# Revit family: PRD_AR_SpprtRls_MEDCAREGrabRail_MEDC0009_MEDC0010_MEDC0011_MEDC0012
name_source: partatom
category: Specialty Equipment
units: mm (PartAtom-declared; Revit-internal decimal feet)

## family parameters
Cut with Voids When Loaded = No
Enable Cutting in Views = No
Host = Face
Maintain Annotation Orientation = No
OmniClass Number = 23.40.20.21.47
OmniClass Title = Bath Grab Bars
Part Type = Normal
Room Calculation Point = No
Round Connector Dimension = Use Diameter
Shared = No

## types (4) — shared parameters
AssetType = Fixed
Back = no
BodyMaterial = PRD_AR_StainlessSteel_SatinFinished_BasaltGrey
Category = Pr_40_20_76_84, Support rails
Color = basalt grey
Default Elevation = 1200 mm
Diameter = 32 mm  [stored 0.104987 ft]
Export Type to IFC As = IfcRailingType
Finish = satin finished
IfcExportAs = IfcRailingType
IfcExportType = HANDRAIL
IsExternal = FALSE
Manufacturer = KWC Group Management AG
ManufacturerName = KWC Group Management AG
ManufacturerURL = www.kwc-professional.com
Material = stainless steel
MaterialCode = 1.4301 Chrome Nickel steel V2A
NBSDescription = Support rails
NBSReference = 45-35-72/360
NominalHeight = 234 mm  [stored 0.767717 ft]
NominalWidth = 113 mm  [stored 0.370735 ft]
OverallHeight = 234 mm
OverallWidth = 113 mm
ProductInformation = http://pim.kwc.com
Status = New
SurfaceFinish = satin finished
Type IFC Predefined Type = HANDRAIL
TypeOfFixing = screw
TypeOfGrabRail = support bar
TypeOfMounting = wall mounting
URL = www.kwc-professional.com
Uniclass2015Code = Pr_40_20_76_84
Uniclass2015Title = Support rails
Uniclass2015Version = Products v1.36
Version = 1
zero-valued in all types: Height

## per-type parameters (varying)
| type | BIMObjectName | Depth | Description | ElectronicFlushActuation | Features | ModelNumber | Name | NominalDepth | OverallDepth | Size |
| MEDC0009 | PRD_AR_SupportRails_MEDCAREFoldingSupportRail_MEDC0009 | 700 mm  [stored 2.29659 ft] | MEDCARE folding support rail with toilet roll holder for wall mounting, stainless steel, basalt grey coated surface, two parallel rail levels, top rail 32 mm, bottom rail 27 mm, material thickness 1.5 mm, plastic end caps, protection against accidental folding, stainless steel mounting plate with basalt grey polyamide cover, load capacity up to 150 kg, mounting material to be provided by client. | No | With toilet roll holder. Load capacity up to 150 kg. Length 700 mm. | 3600003778 | MEDCARE Folding support rail MEDC0009 | 700 mm  [stored 2.29659 ft] | 700 mm | 113 x 234 x 700 mm (W x H x D) |
| MEDC0010 | PRD_AR_SupportRails_MEDCAREFoldingSupportRail_MEDC0010 | 850 mm  [stored 2.78871 ft] | MEDCARE folding support rail with toilet roll holder for wall mounting, stainless steel, basalt grey coated surface, two parallel rail levels, top rail 32 mm, bottom rail 27 mm, material thickness 1.5 mm, plastic end caps, protection against accidental folding, stainless steel mounting plate with basalt grey polyamide cover, load capacity up to 100 kg, mounting material to be provided by client. | No | With toilet roll holder. Load capacity up to 100 kg. Length 850 mm. | 3600003780 | MEDCARE Folding support rail MEDC0010 | 850 mm  [stored 2.78871 ft] | 850 mm | 113 x 234 x 850 mm (W x H x D) |
| MEDC0011 | PRD_AR_SupportRails_MEDCAREFoldingSupportRail_MEDC0011 | 700 mm  [stored 2.29659 ft] | MEDCARE folding support rail with electronic flush actuation, for wall mounting, stainless steel, basalt grey coated surface, two parallel rail levels, upper rail 32 mm, lower rail 27 mm, material thickness 1.5 mm, with plastic end caps and integrated toilet roll holder, protection against unintentional folding, stainless steel mounting plate with basalt grey polyamide cover, load capacity up to 150 kg, mounting material to be provided by client. | Yes | With electronic flush actuation. With toilet roll holder. Load capacity up to 150 kg. Length 700 mm. | 3600003781 | MEDCARE Folding support rail MEDC0011 | 700 mm  [stored 2.29659 ft] | 700 mm | 113 x 234 x 700 mm (W x H x D) |
| MEDC0012 | PRD_AR_SupportRails_MEDCAREFoldingSupportRail_MEDC0012 | 850 mm  [stored 2.78871 ft] | MEDCARE folding support rail with electronic flush actuation, for wall mounting, stainless steel, basalt grey coated surface, two parallel rail levels, upper rail 32 mm, lower rail 27 mm, material thickness 1.5 mm, with plastic end caps and integrated toilet roll holder, protection against unintentional folding, stainless steel mounting plate with basalt grey polyamide cover, load capacity up to 100 kg, mounting material to be provided by client. | Yes | With electronic flush actuation. With toilet roll holder. Load capacity up to 100 kg. Length 850 mm. | 3600003782 | MEDCARE Folding support rail MEDC0012 | 850 mm  [stored 2.78871 ft] | 850 mm | 113 x 234 x 850 mm (W x H x D) |

note: column(s) folded — value = type name in every type: Model, ModelReference

note: [stored X ft] marks values corroborated as IEEE doubles in the binary element streams (Revit-internal decimal feet)

## geometry (parser evidence)
native form markers: Sweep x7
no freeform markers — native parametric forms only
